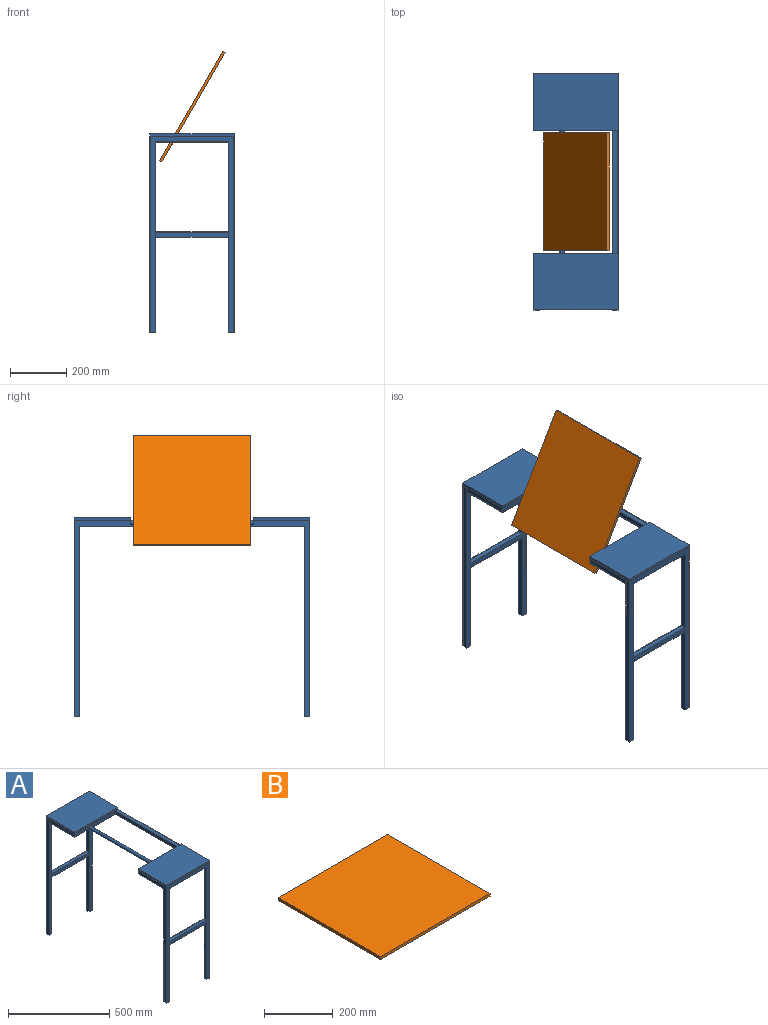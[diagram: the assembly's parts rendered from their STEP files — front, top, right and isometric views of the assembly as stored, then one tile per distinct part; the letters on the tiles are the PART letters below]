
ASSEMBLY  parts=2 mates=1
PART A: 102 faces, bbox 300x840x710 mm
  f0: plane 200x9mm, normal (-1,0,0), area 1800mm2, adj f2,f3,f9,f63
  f1: plane 700x200mm, normal (-1,0,0), area 17600mm2, adj f5,f10,f14,f21,f55,f61
  f2: plane 300x10mm, normal (0,-1,0), area 2720mm2, adj f0,f7,f9,f24,f54,f63
  f3: plane 710x300mm, normal (0,1,0), area 41120mm2, adj f0,f7,f8,f9,f35,f36,f41,f44
  f4: plane 300x10mm, normal (0,1,0), area 2720mm2, adj f7,f11,f12,f24,f53,f62
  f5: plane 710x300mm, normal (0,-1,0), area 41120mm2, adj f1,f7,f11,f12,f15,f16,f21,f25
  f6: plane 280x20mm, normal (0,-1,0), area 5398.9mm2, adj f8,f52,f55,f60,f64
  f7: plane 840x710mm, normal (1,0,0), area 48000mm2, adj f2,f3,f4,f5,f9,f12,f14,f24
  f8: plane 700x200mm, normal (-1,0,0), area 17600mm2, adj f3,f6,f33,f41,f55,f64
  f9: plane 300x200mm, normal (0,0,1), area 60000mm2, adj f0,f2,f3,f7
  f10: plane 280x20mm, normal (0,1,0), area 5398.9mm2, adj f1,f52,f55,f60,f61
  f11: plane 200x9mm, normal (-1,0,0), area 1800mm2, adj f4,f5,f12,f62
  f12: plane 300x200mm, normal (0,0,1), area 60000mm2, adj f4,f5,f7,f11
  f13: plane 260x20mm, normal (0,1,0), area 5200mm2, adj f25,f53,f59,f61
  f14: plane 680x300mm, normal (0,1,0), area 32400mm2, adj f1,f7,f15,f16,f21,f26,f27,f30
  f15: plane 340x20mm, normal (1,0,0), area 6800mm2, adj f5,f14,f21,f32
  f16: plane 320x20mm, normal (1,0,0), area 6400mm2, adj f5,f14,f25,f31
  f17: plane 698.5x297mm, normal (0,1,0), area 28220mm2, adj f18,f20,f21,f22,f23,f28,f29,f30
  f18: plane 698.5x17mm, normal (1,0,0), area 11874.5mm2, adj f17,f19,f21,f22
  f19: plane 698.5x297mm, normal (0,-1,0), area 28220mm2, adj f18,f20,f21,f22,f23,f28,f29,f30
  f20: plane 681.5x17mm, normal (-1,0,0), area 11585.5mm2, adj f17,f19,f21,f23
  f21: plane 20x20mm, normal (0,0,-1), area 111mm2, adj f1,f5,f14,f15,f17,f18,f19,f20
  f22: plane 297x17mm, normal (0,0,-1), area 5049mm2, adj f17,f18,f19,f28
  f23: plane 263x17mm, normal (0,0,1), area 4471mm2, adj f17,f19,f20,f29
  f24: plane 440x20mm, normal (0,0,1), area 8800mm2, adj f2,f4,f7,f52
  f25: plane 260x20mm, normal (0,0,-1), area 5200mm2, adj f5,f13,f16,f26
  f26: plane 320x20mm, normal (-1,0,0), area 6400mm2, adj f5,f14,f25,f31
  f27: plane 340x20mm, normal (-1,0,0), area 6800mm2, adj f5,f14,f30,f32
  f28: plane 698.5x17mm, normal (-1,0,0), area 11874.5mm2, adj f17,f19,f22,f30
  f29: plane 681.5x17mm, normal (1,0,0), area 11585.5mm2, adj f17,f19,f23,f30
  f30: plane 20x20mm, normal (0,0,-1), area 111mm2, adj f5,f7,f14,f17,f19,f27,f28,f29
  f31: plane 260x20mm, normal (0,0,1), area 5200mm2, adj f5,f14,f16,f26
  f32: plane 260x20mm, normal (0,0,-1), area 5200mm2, adj f5,f14,f15,f27
  f33: plane 680x300mm, normal (0,-1,0), area 32400mm2, adj f7,f8,f35,f36,f41,f45,f46,f49
  f34: plane 260x20mm, normal (0,-1,0), area 5200mm2, adj f44,f54,f56,f64
  f35: plane 340x20mm, normal (1,0,0), area 6800mm2, adj f3,f33,f41,f51
  f36: plane 320x20mm, normal (1,0,0), area 6400mm2, adj f3,f33,f44,f50
  f37: plane 698.5x297mm, normal (0,-1,0), area 28220mm2, adj f38,f40,f41,f42,f43,f47,f48,f49
  f38: plane 698.5x17mm, normal (1,0,0), area 11874.5mm2, adj f37,f39,f41,f42
  f39: plane 698.5x297mm, normal (0,1,0), area 28220mm2, adj f38,f40,f41,f42,f43,f47,f48,f49
  f40: plane 681.5x17mm, normal (-1,0,0), area 11585.5mm2, adj f37,f39,f41,f43
  f41: plane 20x20mm, normal (0,0,-1), area 111mm2, adj f3,f8,f33,f35,f37,f38,f39,f40
  f42: plane 297x17mm, normal (0,0,-1), area 5049mm2, adj f37,f38,f39,f47
  f43: plane 263x17mm, normal (0,0,1), area 4471mm2, adj f37,f39,f40,f48
  f44: plane 260x20mm, normal (0,0,-1), area 5200mm2, adj f3,f34,f36,f45
  f45: plane 320x20mm, normal (-1,0,0), area 6400mm2, adj f3,f33,f44,f50
  f46: plane 340x20mm, normal (-1,0,0), area 6800mm2, adj f3,f33,f49,f51
  f47: plane 698.5x17mm, normal (-1,0,0), area 11874.5mm2, adj f37,f39,f42,f49
  f48: plane 681.5x17mm, normal (1,0,0), area 11585.5mm2, adj f37,f39,f43,f49
  f49: plane 20x20mm, normal (0,0,-1), area 111mm2, adj f3,f7,f33,f37,f39,f46,f47,f48
  f50: plane 260x20mm, normal (0,0,1), area 5200mm2, adj f3,f33,f36,f45
  f51: plane 260x20mm, normal (0,0,-1), area 5200mm2, adj f3,f33,f35,f46
  f52: plane 440x20mm, normal (-1,0,0), area 8800mm2, adj f6,f10,f24,f55
  f53: plane 200x21mm, normal (-1,0,0), area 3400mm2, adj f4,f5,f13,f55,f58,f61,f62
  f54: plane 200x21mm, normal (-1,0,0), area 3400mm2, adj f2,f3,f34,f55,f57,f63,f64
  f55: plane 800x300mm, normal (0,0,-1), area 33600mm2, adj f1,f6,f7,f8,f10,f14,f33,f52
  f56: plane 160x20mm, normal (1,0,0), area 3200mm2, adj f34,f55,f57,f64
  f57: plane 260x20mm, normal (0,1,0), area 5200mm2, adj f54,f55,f56,f64
  f58: plane 260x20mm, normal (0,-1,0), area 5200mm2, adj f53,f55,f59,f61
  f59: plane 160x20mm, normal (1,0,0), area 3200mm2, adj f13,f55,f58,f61
  f60: cylinder r=8mm len=440mm, axis (0,-1,0), area 22116.8mm2, adj f6,f10
  f61: plane 280x200mm, normal (0,0,1), area 14400mm2, adj f1,f5,f10,f13,f53,f58,f59
  f62: plane 280x200mm, normal (0,0,-1), area 56000mm2, adj f4,f5,f11,f53
  f63: plane 280x200mm, normal (0,0,-1), area 56000mm2, adj f0,f2,f3,f54
  f64: plane 280x200mm, normal (0,0,1), area 14400mm2, adj f3,f6,f8,f34,f54,f56,f57
  f65: plane 17x17mm, normal (0,-1,0), area 289mm2, adj f66,f67,f68,f69
  f66: plane 800x17mm, normal (-1,0,0), area 13600mm2, adj f65,f67,f69,f70
  f67: plane 800x17mm, normal (0,0,1), area 13600mm2, adj f65,f66,f68,f70
  f68: plane 800x17mm, normal (1,0,0), area 13600mm2, adj f65,f67,f69,f70
  f69: plane 800x17mm, normal (0,0,-1), area 13600mm2, adj f65,f66,f68,f70
  f70: plane 17x17mm, normal (0,1,0), area 289mm2, adj f66,f67,f68,f69
  f71: plane 17x17mm, normal (-1,0,0), area 289mm2, adj f72,f73,f76,f77
  f72: plane 278.5x17mm, normal (0,-1,0), area 4734.5mm2, adj f71,f75,f76,f77
  f73: plane 261.5x17mm, normal (0,1,0), area 4445.5mm2, adj f71,f74,f76,f77
  f74: plane 161.5x17mm, normal (-1,0,0), area 2745.5mm2, adj f73,f76,f77,f78
  f75: plane 178.5x17mm, normal (1,0,0), area 3034.5mm2, adj f72,f76,f77,f78
  f76: plane 278.5x178.5mm, normal (0,0,1), area 7480mm2, adj f71,f72,f73,f74,f75,f78
  f77: plane 278.5x178.5mm, normal (0,0,-1), area 7480mm2, adj f71,f72,f73,f74,f75,f78
  f78: plane 17x17mm, normal (0,1,0), area 289mm2, adj f74,f75,f76,f77
  f79: plane 17x17mm, normal (-1,0,0), area 289mm2, adj f80,f81,f82,f83
  f80: plane 260x17mm, normal (0,0,1), area 4420mm2, adj f79,f81,f83,f84
  f81: plane 260x17mm, normal (0,-1,0), area 4420mm2, adj f79,f80,f82,f84
  f82: plane 260x17mm, normal (0,0,-1), area 4420mm2, adj f79,f81,f83,f84
  f83: plane 260x17mm, normal (0,1,0), area 4420mm2, adj f79,f80,f82,f84
  f84: plane 17x17mm, normal (1,0,0), area 289mm2, adj f80,f81,f82,f83
  f85: plane 17x17mm, normal (-1,0,0), area 289mm2, adj f86,f87,f89,f91
  f86: plane 278.5x17mm, normal (0,1,0), area 4734.5mm2, adj f85,f89,f90,f91
  f87: plane 261.5x17mm, normal (0,-1,0), area 4445.5mm2, adj f85,f88,f89,f91
  f88: plane 161.5x17mm, normal (-1,0,0), area 2745.5mm2, adj f87,f89,f91,f92
  f89: plane 278.5x178.5mm, normal (0,0,1), area 7480mm2, adj f85,f86,f87,f88,f90,f92
  f90: plane 178.5x17mm, normal (1,0,0), area 3034.5mm2, adj f86,f89,f91,f92
  f91: plane 278.5x178.5mm, normal (0,0,-1), area 7480mm2, adj f85,f86,f87,f88,f90,f92
  f92: plane 17x17mm, normal (0,-1,0), area 289mm2, adj f88,f89,f90,f91
  f93: plane 17x17mm, normal (-1,0,0), area 289mm2, adj f94,f95,f96,f97
  f94: plane 260x17mm, normal (0,0,1), area 4420mm2, adj f93,f95,f97,f98
  f95: plane 260x17mm, normal (0,1,0), area 4420mm2, adj f93,f94,f96,f98
  f96: plane 260x17mm, normal (0,0,-1), area 4420mm2, adj f93,f95,f97,f98
  f97: plane 260x17mm, normal (0,-1,0), area 4420mm2, adj f93,f94,f96,f98
  f98: plane 17x17mm, normal (1,0,0), area 289mm2, adj f94,f95,f96,f97
  f99: cylinder r=6.5mm len=440mm, axis (0,-1,0), area 17969.9mm2, adj f100,f101
  f100: plane 13x13mm, normal (0,1,0), area 132.7mm2, adj f99
  f101: plane 13x13mm, normal (0,-1,0), area 132.7mm2, adj f99
PART B: 14 faces, bbox 450x420x28 mm
  f0: plane 450x420mm, normal (0,0,-1), area 188687.2mm2, adj f1,f2,f3,f4,f6,f7,f8,f9
  f1: plane 450x10mm, normal (0,1,0), area 4500mm2, adj f0,f2,f4,f5
  f2: plane 420x10mm, normal (-1,0,0), area 4200mm2, adj f0,f1,f3,f5
  f3: plane 450x10mm, normal (0,-1,0), area 4500mm2, adj f0,f2,f4,f5
  f4: plane 420x10mm, normal (1,0,0), area 4200mm2, adj f0,f1,f3,f5
  f5: plane 450x420mm, normal (0,0,1), area 189000mm2, adj f1,f2,f3,f4
  f6: cylinder r=8.5mm len=25mm, axis (0,-1,0), area 1188.7mm2, adj f0,f8,f9
  f7: cylinder r=10mm len=25mm, axis (0,-1,0), area 1249mm2, adj f0,f8,f9
  f8: plane 20x18mm, normal (0,1,0), area 72.8mm2, adj f0,f6,f7
  f9: plane 20x18mm, normal (0,-1,0), area 72.8mm2, adj f0,f6,f7
  f10: cylinder r=8.5mm len=25mm, axis (0,1,0), area 1188.7mm2, adj f0,f12,f13
  f11: cylinder r=10mm len=25mm, axis (0,1,0), area 1249mm2, adj f0,f12,f13
  f12: plane 20x18mm, normal (0,-1,0), area 72.8mm2, adj f0,f10,f11
  f13: plane 20x18mm, normal (0,1,0), area 72.8mm2, adj f0,f10,f11
PLACE A at identity fixed
PLACE B rot(axis=(0,-1,0),60deg) t=(271.18,0,214.3)mm
MATE revolute B.f6 <-> A.f60  axis (0,-1,0) through (-50,-180,342)mm
